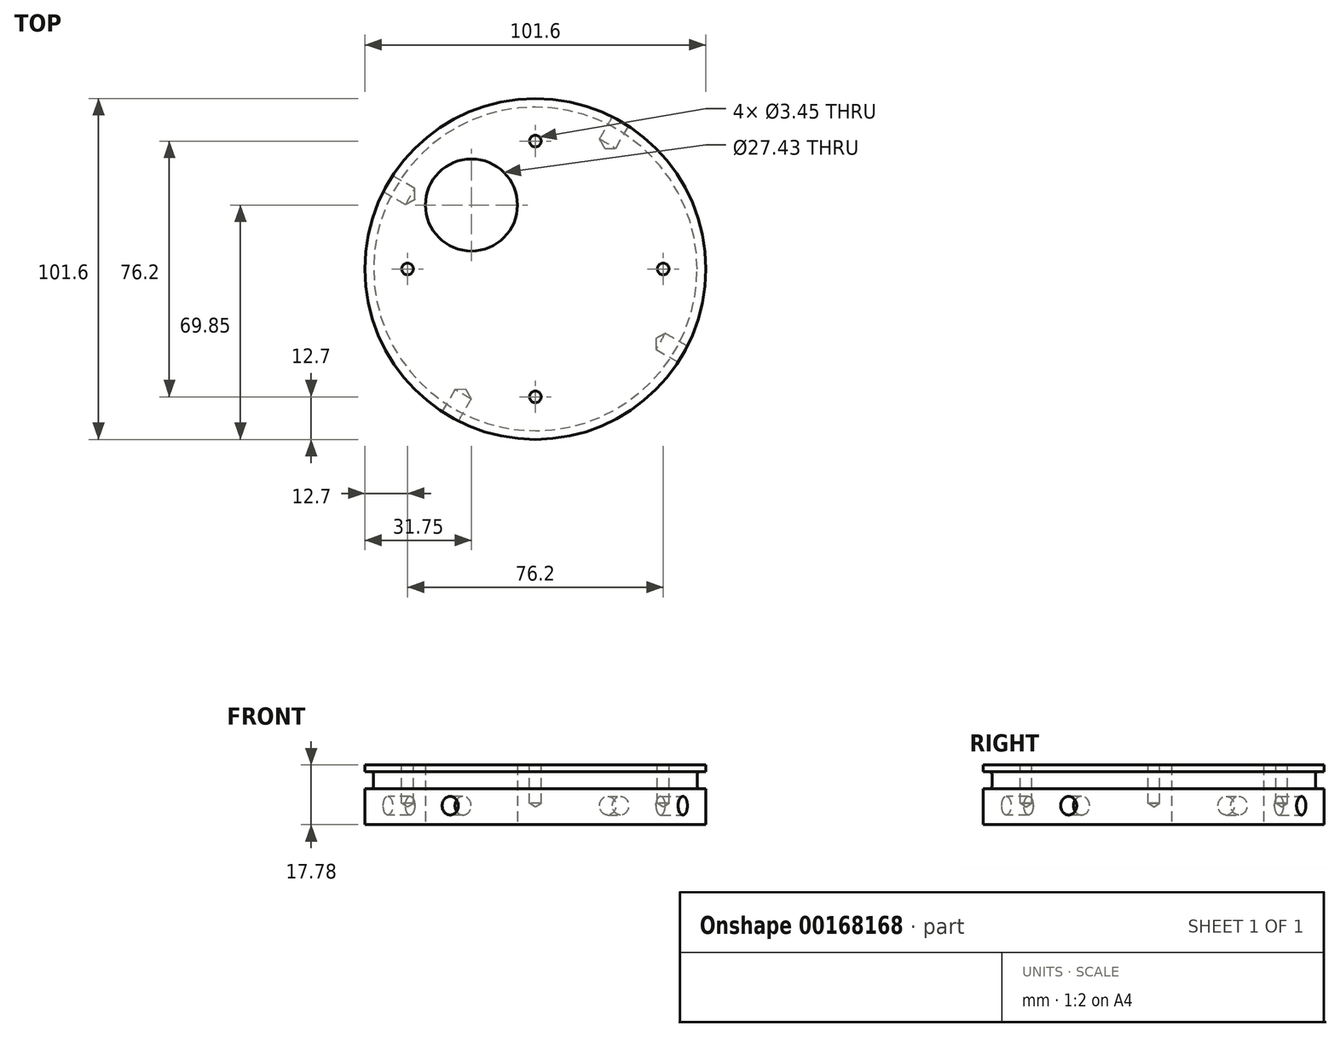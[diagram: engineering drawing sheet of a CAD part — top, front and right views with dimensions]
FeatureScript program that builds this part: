
annotation { "Feature Type Name" : "Feature", "Feature Type Description" : "" }
export const myFeature = defineFeature(function(context is Context, id is Id, definition is map)
    precondition{}
    {
        {
            var Q0;
            Q0=qCreatedBy(makeId("Top.planeOp"),FACE);
            var sketch = newSketch(context, id + "F0", { "sketchPlane" : qUnion([Q0])});
            skCircle(sketch, "E0", {"center": v(0, 0) * mm, "radius": 50.8 * mm});
            skSolve(sketch);
        }
        {
            var Q0;
            Q0=makeQuery(id+"F0.imprint","IMPRINT",FACE,{"disambiguationData":[TD([[makeQuery(id+"F0.imprint","IMPRINT",EDGE,{"derivedFrom":sQuery(id+"F0.wireOp",EDGE,"E0")}),1.0]])]});
            extrude(context, id + "F1", {"entities" : qUnion([Q0]), "depth" : 17.78 * mm});
        }
        {
            var Q0;
            {var subQ0=makeQuery(id+"FhJubWmbG7UBd7M_1.boolean.opBoolean","COPY",FACE,{"derivedFrom":makeQuery(id+"FhJubWmbG7UBd7M_1.opExtrude","SWEPT_FACE",FACE,{"disambiguationData":[OSD([sQuery(id+"FRuIeaWD6VeLny9_1.wireOp",EDGE,"idePJaX5-tPPE-BKw2-N1m4-zZUQrY6AHjir")])]})});Q0=makeQuery(id+"FOQC5dfjhO448EJ_1.boolean.opBoolean","SPLIT",FACE,{"disambiguationData":[TD([subQ0])],"derivedFrom":makeQuery(id+"FkcieFRIapZdHPD_1.boolean.opBoolean","SPLIT",FACE,{"disambiguationData":[TD([subQ0])],"derivedFrom":makeQuery(id+"F1.opExtrude","CAP_FACE",FACE,{"disambiguationData":[OSD([sQuery(id+"F0.wireOp",EDGE,"E0")])],"isStart":false})})});}
            var sketch = newSketch(context, id + "F2", { "sketchPlane" : qUnion([Q0])});
            skCircle(sketch, "E1", {"center": v(0, 0) * mm, "radius": 38.1 * mm, "construction": true});
            skLineSegment(sketch, "E2", {"start": v(0, 0) * mm, "end": v(38.1, 0) * mm, "construction": true});
            skPoint(sketch, "E3", {"position": v(38.1, 0) * mm});
            skPoint(sketch, "E4.1.0", {"position": v(0, 38.1) * mm});
            skPoint(sketch, "E4.2.0", {"position": v(-38.1, 0) * mm});
            skPoint(sketch, "E4.3.0", {"position": v(0, -38.1) * mm});
            skSolve(sketch);
        }
        {
            var Q0;
            Q0=sQuery(id+"F2.wireOp",VERTEX,"E3");
            var Q1;
            Q1=sQuery(id+"F2.wireOp",VERTEX,"E4.3.0");
            var Q2;
            Q2=sQuery(id+"F2.wireOp",VERTEX,"E4.2.0");
            var Q3;
            Q3=sQuery(id+"F2.wireOp",VERTEX,"E4.1.0");
            var Q4;
            Q4=makeQuery(id+"F1.opExtrude","SWEPT_BODY",BODY,{"disambiguationData":[OSD([sQuery(id+"F0.wireOp",EDGE,"E0")])]});
            hole(context, id + "F3", {"style" : HoleStyle.SIMPLE, "endStyle" : HoleEndStyle.BLIND, "standardTappedOrClearance" : lookupTablePath({ "standard" : "ANSI", "engagement" : "75%", "pitch" : "32 tpi", "size" : "#8", "type" : "Tapped" }), "standardBlindInLast" : lookupTablePath({ "standard" : "ANSI", "engagement" : "75%", "pitch" : "32 tpi", "size" : "#8", "type" : "Tapped" }), "holeDiameter" : 3.45 * mm, "holeDepth" : 11.43 * mm, "locations" : qUnion([Q0, Q1, Q2, Q3]), "scope" : qUnion([Q4]), "majorDiameter" : 4.17 * mm});
        }
        {
            var Q0;
            Q0=makeQuery(id+"FOQC5dfjhO448EJ_1.boolean.opBoolean","SPLIT",FACE,{"disambiguationData":[TD([makeQuery(id+"FhJubWmbG7UBd7M_1.boolean.opBoolean","COPY",FACE,{"derivedFrom":makeQuery(id+"FhJubWmbG7UBd7M_1.opExtrude","SWEPT_FACE",FACE,{"disambiguationData":[OSD([sQuery(id+"FRuIeaWD6VeLny9_1.wireOp",EDGE,"idePJaX5-tPPE-BKw2-N1m4-zZUQrY6AHjir")])]})})])],"derivedFrom":makeQuery(id+"F1.opExtrude","CAP_FACE",FACE,{"disambiguationData":[OSD([sQuery(id+"F0.wireOp",EDGE,"E0")])],"isStart":false})});
            cPlane(context, id + "F4", {"entities" : qUnion([Q0]), "cplaneType" : CPlaneType.OFFSET, "offset" : 2.03 * mm, "oppositeDirection" : true, "width" : 152.4 * mm, "height" : 152.4 * mm});
        }
        {
            var Q0;
            Q0=qCreatedBy(id+"F4.planeOp",FACE);
            var sketch = newSketch(context, id + "F5", { "sketchPlane" : qUnion([Q0])});
            skCircle(sketch, "E5", {"center": v(0, 0) * mm, "radius": 48.2 * mm});
            skCircle(sketch, "E6.0", {"center": v(0, 0) * mm, "radius": 50.8 * mm});
            skSolve(sketch);
        }
        {
            var Q0;
            Q0=qSketchRegion(id+"F5",true);
            extrude(context, id + "F6", {"entities" : qUnion([Q0]), "operationType" : NewBodyOperationType.REMOVE, "oppositeDirection" : true, "depth" : 5 * mm});
        }
        {
            var Q0;
            Q0=makeQuery(id+"F6.boolean.opBoolean","COPY",EDGE,{"derivedFrom":makeQuery(id+"F6.opExtrude","CAP_EDGE",EDGE,{"disambiguationData":[OSD([sQuery(id+"F5.wireOp",EDGE,"E5")])],"isStart":false})});
            var Q1;
            Q1=makeQuery(id+"F6.boolean.opBoolean","COPY",EDGE,{"derivedFrom":makeQuery(id+"F6.opExtrude","CAP_EDGE",EDGE,{"disambiguationData":[OSD([sQuery(id+"F5.wireOp",EDGE,"E5")])],"isStart":true})});
            fillet(context, id + "F7", {"entities" : qUnion([Q0, Q1]), "radius" : 0.76 * mm, "tangentPropagation" : true, "allowEdgeOverflow" : false});
        }
        {
            var Q0;
            {var subQ1=sQuery(id+"F0.wireOp",EDGE,"E0");var subQ2=makeQuery(id+"F1.opExtrude","SWEPT_FACE",FACE,{"disambiguationData":[OSD([subQ1])]});Q0=makeQuery(id+"FkcieFRIapZdHPD_1.boolean.opBoolean","SPLIT",FACE,{"disambiguationData":[TD([subQ2])],"derivedFrom":makeQuery(id+"F1.opExtrude","CAP_FACE",FACE,{"disambiguationData":[OSD([subQ1])],"isStart":false})});}
            var sketch = newSketch(context, id + "F8", { "sketchPlane" : qUnion([Q0])});
            skCircle(sketch, "E7.0", {"center": v(0, 0) * mm, "radius": 50.8 * mm, "construction": true});
            skPoint(sketch, "E8", {"position": v(-25.4, -44) * mm});
            skLineSegment(sketch, "E9", {"start": v(0, -50.8) * mm, "end": v(0, 0) * mm, "construction": true});
            skLineSegment(sketch, "E10", {"start": v(0, 0) * mm, "end": v(-17.96, -31.1) * mm, "construction": true});
            skLineSegment(sketch, "E11", {"start": v(-17.96, -31.1) * mm, "end": v(-25.4, -44) * mm, "construction": true});
            skLineSegment(sketch, "E12", {"start": v(0, 0) * mm, "end": v(25.4, 44) * mm, "construction": true});
            skLineSegment(sketch, "E13", {"start": v(25.4, 44) * mm, "end": v(0, 0) * mm, "construction": true});
            skLineSegment(sketch, "E14", {"start": v(44, -25.4) * mm, "end": v(0, 0) * mm, "construction": true});
            skLineSegment(sketch, "E15", {"start": v(0, 0) * mm, "end": v(-44, 25.4) * mm, "construction": true});
            skPoint(sketch, "E16", {"position": v(25.4, 44) * mm});
            skPoint(sketch, "E17", {"position": v(44, -25.4) * mm});
            skPoint(sketch, "E18", {"position": v(-44, 25.4) * mm});
            skSolve(sketch);
        }
        {
            var Q0;
            Q0=qCreatedBy(makeId("Front.planeOp"),FACE);
            var sketch = newSketch(context, id + "F9", { "sketchPlane" : qUnion([Q0])});
            skLineSegment(sketch, "E19", {"start": v(0, 0) * mm, "end": v(0, 38.57) * mm, "construction": true});
            skSolve(sketch);
        }
        {
            var Q0;
            Q0=sQuery(id+"F9.wireOp",EDGE,"E19");
            cPlane(context, id + "F10", {"entities" : qUnion([Q0]), "cplaneType" : CPlaneType.LINE_ANGLE, "offset" : 25.4 * mm, "angle" : 60 * degree, "width" : 152.4 * mm, "height" : 152.4 * mm});
        }
        {
            var Q0;
            Q0=sQuery(id+"F8.wireOp",VERTEX,"E8");
            var Q1;
            Q1=qCreatedBy(id+"F10.planeOp",FACE);
            cPlane(context, id + "F11", {"entities" : qUnion([Q0, Q1]), "cplaneType" : CPlaneType.PLANE_POINT, "offset" : 25.4 * mm, "width" : 152.4 * mm, "height" : 152.4 * mm});
        }
        {
            var Q0;
            Q0=qCreatedBy(id+"F11.planeOp",FACE);
            var Q1;
            Q1=sQuery(id+"F8.wireOp",VERTEX,"E16");
            cPlane(context, id + "F12", {"entities" : qUnion([Q0, Q1]), "cplaneType" : CPlaneType.PLANE_POINT, "offset" : 25.4 * mm, "width" : 152.4 * mm, "height" : 152.4 * mm});
        }
        {
            var Q0;
            Q0=sQuery(id+"F9.wireOp",EDGE,"E19");
            cPlane(context, id + "F13", {"entities" : qUnion([Q0]), "cplaneType" : CPlaneType.LINE_ANGLE, "offset" : 25.4 * mm, "angle" : 150 * degree, "width" : 152.4 * mm, "height" : 152.4 * mm});
        }
        {
            var Q0;
            Q0=sQuery(id+"F8.wireOp",VERTEX,"E18");
            var Q1;
            Q1=qCreatedBy(id+"F13.planeOp",FACE);
            cPlane(context, id + "F14", {"entities" : qUnion([Q0, Q1]), "cplaneType" : CPlaneType.PLANE_POINT, "offset" : 25.4 * mm, "width" : 152.4 * mm, "height" : 152.4 * mm});
        }
        {
            var Q0;
            Q0=qCreatedBy(id+"F13.planeOp",FACE);
            var Q1;
            Q1=sQuery(id+"F8.wireOp",VERTEX,"E17");
            cPlane(context, id + "F15", {"entities" : qUnion([Q0, Q1]), "cplaneType" : CPlaneType.PLANE_POINT, "offset" : 25.4 * mm, "width" : 152.4 * mm, "height" : 152.4 * mm});
        }
        {
            var Q0;
            Q0=qCreatedBy(id+"F11.planeOp",FACE);
            var sketch = newSketch(context, id + "F16", { "sketchPlane" : qUnion([Q0])});
            skLineSegment(sketch, "E20", {"start": v(0, 0) * mm, "end": v(0, 5.66) * mm, "construction": true});
            skPoint(sketch, "E21", {"position": v(0, 5.66) * mm});
            skSolve(sketch);
        }
        {
            var Q0;
            Q0=qCreatedBy(id+"F12.planeOp",FACE);
            var sketch = newSketch(context, id + "F17", { "sketchPlane" : qUnion([Q0])});
            skPoint(sketch, "E22", {"position": v(0, 5.66) * mm});
            skLineSegment(sketch, "E23.0", {"start": v(0, 0) * mm, "end": v(0, 5.66) * mm, "construction": true});
            skSolve(sketch);
        }
        {
            var Q0;
            Q0=qCreatedBy(id+"F14.planeOp",FACE);
            var sketch = newSketch(context, id + "F18", { "sketchPlane" : qUnion([Q0])});
            skLineSegment(sketch, "E24", {"start": v(0, 0) * mm, "end": v(0, 5.66) * mm, "construction": true});
            skLineSegment(sketch, "E25.0", {"start": v(-50.8, 0) * mm, "end": v(-50.8, 5.66) * mm, "construction": true});
            skPoint(sketch, "E26", {"position": v(0, 5.66) * mm});
            skLineSegment(sketch, "E27", {"start": v(-50.8, 5.66) * mm, "end": v(0, 5.66) * mm, "construction": true});
            skSolve(sketch);
        }
        {
            var Q0;
            Q0=qCreatedBy(id+"F15.planeOp",FACE);
            var sketch = newSketch(context, id + "F19", { "sketchPlane" : qUnion([Q0])});
            skLineSegment(sketch, "E28.0", {"start": v(0, 0) * mm, "end": v(0, 5.66) * mm, "construction": true});
            skPoint(sketch, "E29", {"position": v(0, 5.66) * mm});
            skSolve(sketch);
        }
        {
            var Q0;
            Q0=sQuery(id+"F19.wireOp",VERTEX,"E29");
            var Q1;
            Q1=makeQuery(id+"F1.opExtrude","SWEPT_BODY",BODY,{"disambiguationData":[OSD([sQuery(id+"F0.wireOp",EDGE,"E0")])]});
            hole(context, id + "F20", {"style" : HoleStyle.SIMPLE, "endStyle" : HoleEndStyle.BLIND, "oppositeDirection" : true, "standardTappedOrClearance" : lookupTablePath({ "standard" : "ANSI", "engagement" : "75%", "pitch" : "32 tpi", "size" : "1/4", "type" : "Tapped" }), "standardBlindInLast" : lookupTablePath({ "standard" : "ANSI", "engagement" : "75%", "pitch" : "32 tpi", "size" : "1/4", "type" : "Tapped" }), "holeDiameter" : 5.56 * mm, "holeDepth" : 7.62 * mm, "locations" : qUnion([Q0]), "scope" : qUnion([Q1]), "majorDiameter" : 6.35 * mm});
        }
        {
            var Q0;
            Q0=sQuery(id+"F18.wireOp",VERTEX,"E26");
            var Q1;
            Q1=makeQuery(id+"F1.opExtrude","SWEPT_BODY",BODY,{"disambiguationData":[OSD([sQuery(id+"F0.wireOp",EDGE,"E0")])]});
            hole(context, id + "F21", {"style" : HoleStyle.SIMPLE, "endStyle" : HoleEndStyle.BLIND, "standardTappedOrClearance" : lookupTablePath({ "standard" : "ANSI", "engagement" : "75%", "pitch" : "32 tpi", "size" : "1/4", "type" : "Tapped" }), "standardBlindInLast" : lookupTablePath({ "standard" : "ANSI", "engagement" : "75%", "pitch" : "32 tpi", "size" : "1/4", "type" : "Tapped" }), "holeDiameter" : 5.56 * mm, "holeDepth" : 7.62 * mm, "locations" : qUnion([Q0]), "scope" : qUnion([Q1]), "majorDiameter" : 6.35 * mm});
        }
        {
            var Q0;
            Q0=sQuery(id+"F16.wireOp",VERTEX,"E21");
            var Q1;
            Q1=makeQuery(id+"F1.opExtrude","SWEPT_BODY",BODY,{"disambiguationData":[OSD([sQuery(id+"F0.wireOp",EDGE,"E0")])]});
            hole(context, id + "F22", {"style" : HoleStyle.SIMPLE, "endStyle" : HoleEndStyle.BLIND, "oppositeDirection" : true, "standardTappedOrClearance" : lookupTablePath({ "standard" : "ANSI", "engagement" : "75%", "pitch" : "32 tpi", "size" : "1/4", "type" : "Tapped" }), "standardBlindInLast" : lookupTablePath({ "standard" : "ANSI", "engagement" : "75%", "pitch" : "32 tpi", "size" : "1/4", "type" : "Tapped" }), "holeDiameter" : 5.56 * mm, "holeDepth" : 7.62 * mm, "locations" : qUnion([Q0]), "scope" : qUnion([Q1]), "majorDiameter" : 6.35 * mm});
        }
        {
            var Q0;
            Q0=sQuery(id+"F17.wireOp",VERTEX,"E22");
            var Q1;
            Q1=makeQuery(id+"F1.opExtrude","SWEPT_BODY",BODY,{"disambiguationData":[OSD([sQuery(id+"F0.wireOp",EDGE,"E0")])]});
            hole(context, id + "F23", {"style" : HoleStyle.SIMPLE, "endStyle" : HoleEndStyle.BLIND, "standardTappedOrClearance" : lookupTablePath({ "standard" : "ANSI", "engagement" : "75%", "pitch" : "32 tpi", "size" : "1/4", "type" : "Tapped" }), "standardBlindInLast" : lookupTablePath({ "standard" : "ANSI", "engagement" : "75%", "pitch" : "32 tpi", "size" : "1/4", "type" : "Tapped" }), "holeDiameter" : 5.56 * mm, "holeDepth" : 7.62 * mm, "locations" : qUnion([Q0]), "scope" : qUnion([Q1]), "majorDiameter" : 6.35 * mm});
        }
        {
            var Q0;
            Q0=makeQuery(id+"F1.opExtrude","CAP_FACE",FACE,{"disambiguationData":[OSD([sQuery(id+"F0.wireOp",EDGE,"E0")])],"isStart":true});
            var sketch = newSketch(context, id + "F24", { "sketchPlane" : qUnion([Q0])});
            skCircle(sketch, "E30.0", {"center": v(-38.1, 0) * mm, "radius": 1.73 * mm, "construction": true});
            skCircle(sketch, "E31.0", {"center": v(0, -38.1) * mm, "radius": 1.73 * mm, "construction": true});
            skLineSegment(sketch, "E32", {"start": v(-38.1, 0) * mm, "end": v(0, -38.1) * mm, "construction": true});
            skPoint(sketch, "E33", {"position": v(-19.05, -19.05) * mm});
            skSolve(sketch);
        }
        {
            var Q0;
            Q0=sQuery(id+"F24.wireOp",VERTEX,"E33");
            var Q1;
            Q1=makeQuery(id+"F1.opExtrude","SWEPT_BODY",BODY,{"disambiguationData":[OSD([sQuery(id+"F0.wireOp",EDGE,"E0")])]});
            hole(context, id + "F25", {"style" : HoleStyle.SIMPLE, "endStyle" : HoleEndStyle.THROUGH, "holeDiameter" : 27.43 * mm, "locations" : qUnion([Q0]), "scope" : qUnion([Q1]), "isTappedThrough" : true});
        }
    });
